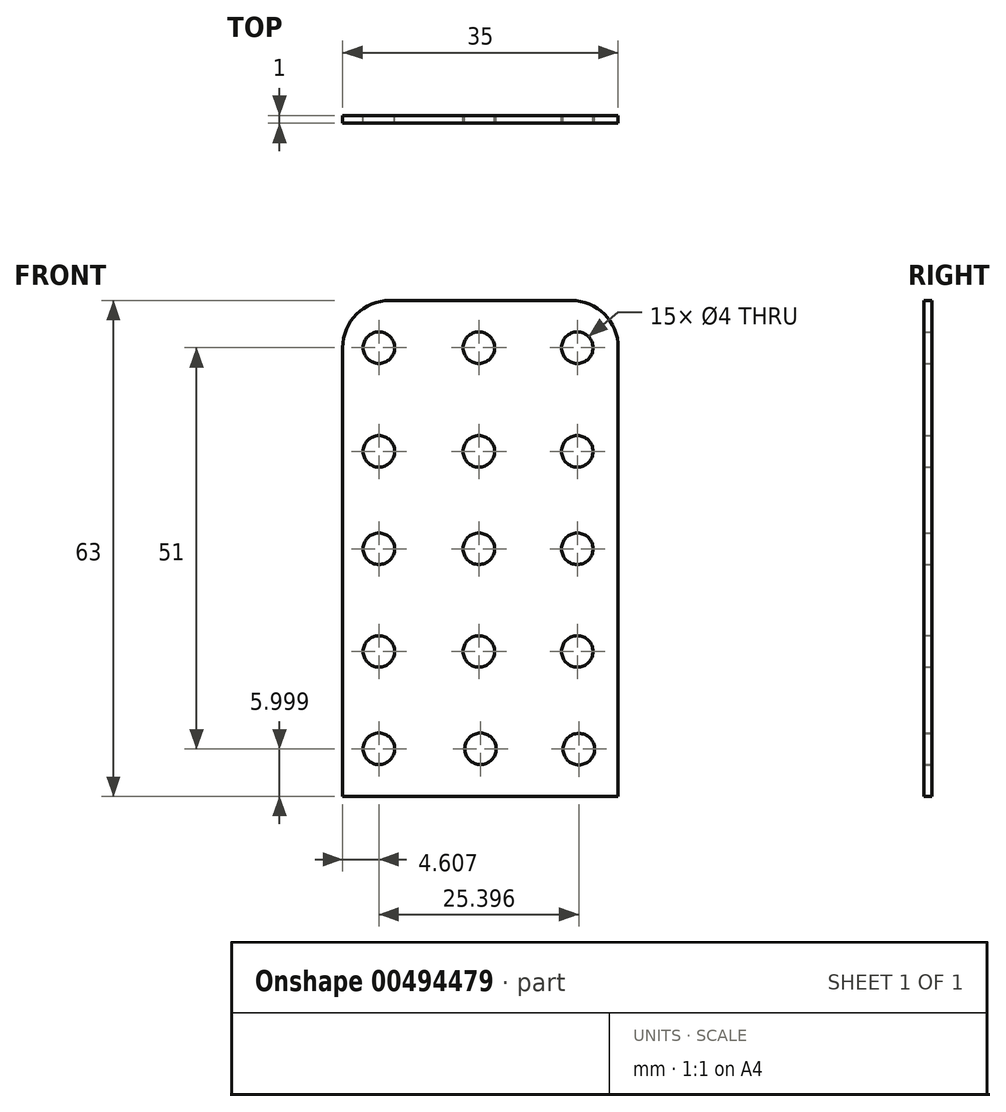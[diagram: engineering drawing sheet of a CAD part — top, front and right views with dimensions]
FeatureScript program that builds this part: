
annotation { "Feature Type Name" : "Feature", "Feature Type Description" : "" }
export const myFeature = defineFeature(function(context is Context, id is Id, definition is map)
    precondition{}
    {
        {
            var Q0;
            Q0=qCreatedBy(makeId("Front.planeOp"),FACE);
            var sketch = newSketch(context, id + "F0", { "sketchPlane" : qUnion([Q0])});
            skLineSegment(sketch, "E0", {"start": v(-29.34, -21.47) * mm, "end": v(-29.34, 35.53) * mm});
            skLineSegment(sketch, "E1", {"start": v(-23.34, 41.53) * mm, "end": v(-0.34, 41.53) * mm});
            skLineSegment(sketch, "E2", {"start": v(5.66, 35.53) * mm, "end": v(5.66, -21.47) * mm});
            skLineSegment(sketch, "E3", {"start": v(-29.34, -21.47) * mm, "end": v(5.66, -21.47) * mm});
            skPoint(sketch, "E4.visualSharp", {"position": v(-29.34, 41.53) * mm});
            skArc(sketch, "E4.filletArc", {"start": v(-23.34, 41.53) * mm, "mid": v(-27.58, 39.77) * mm, "end": v(-29.34, 35.53) * mm});
            skPoint(sketch, "E5.visualSharp", {"position": v(5.66, 41.53) * mm});
            skArc(sketch, "E5.filletArc", {"start": v(5.66, 35.53) * mm, "mid": v(3.9, 39.77) * mm, "end": v(-0.34, 41.53) * mm});
            skCircle(sketch, "E6", {"center": v(0.66, -15.47) * mm, "radius": 2 * mm});
            skCircle(sketch, "E7", {"center": v(-24.73, -15.43) * mm, "radius": 2 * mm});
            skLineSegment(sketch, "E8", {"start": v(5.66, -21.47) * mm, "end": v(-11.84, -21.47) * mm});
            skCircle(sketch, "E9", {"center": v(-11.84, -15.43) * mm, "radius": 2 * mm});
            skCircle(sketch, "E10", {"center": v(0.46, -3.06) * mm, "radius": 2 * mm});
            skCircle(sketch, "E11", {"center": v(-24.73, -3.06) * mm, "radius": 2 * mm});
            skCircle(sketch, "E12", {"center": v(-12.04, -3.06) * mm, "radius": 2 * mm});
            skCircle(sketch, "E13", {"center": v(0.47, 9.98) * mm, "radius": 2 * mm});
            skCircle(sketch, "E14", {"center": v(-24.73, 9.98) * mm, "radius": 2 * mm});
            skCircle(sketch, "E15", {"center": v(-12.03, 9.98) * mm, "radius": 2 * mm});
            skCircle(sketch, "E16", {"center": v(0.46, 22.35) * mm, "radius": 2 * mm});
            skCircle(sketch, "E17", {"center": v(-24.73, 22.35) * mm, "radius": 2 * mm});
            skCircle(sketch, "E18", {"center": v(-12.04, 22.35) * mm, "radius": 2 * mm});
            skCircle(sketch, "E19", {"center": v(0.46, 35.53) * mm, "radius": 2 * mm});
            skCircle(sketch, "E20", {"center": v(-24.73, 35.53) * mm, "radius": 2 * mm});
            skCircle(sketch, "E21", {"center": v(-12.04, 35.53) * mm, "radius": 2 * mm});
            skSolve(sketch);
        }
        {
            var Q0;
            Q0 = qSketchRegion(id + "F0", true);
            extrude(context, id + "F1", {"entities" : qUnion([Q0]), "depth" : 1 * mm});
        }
    });
